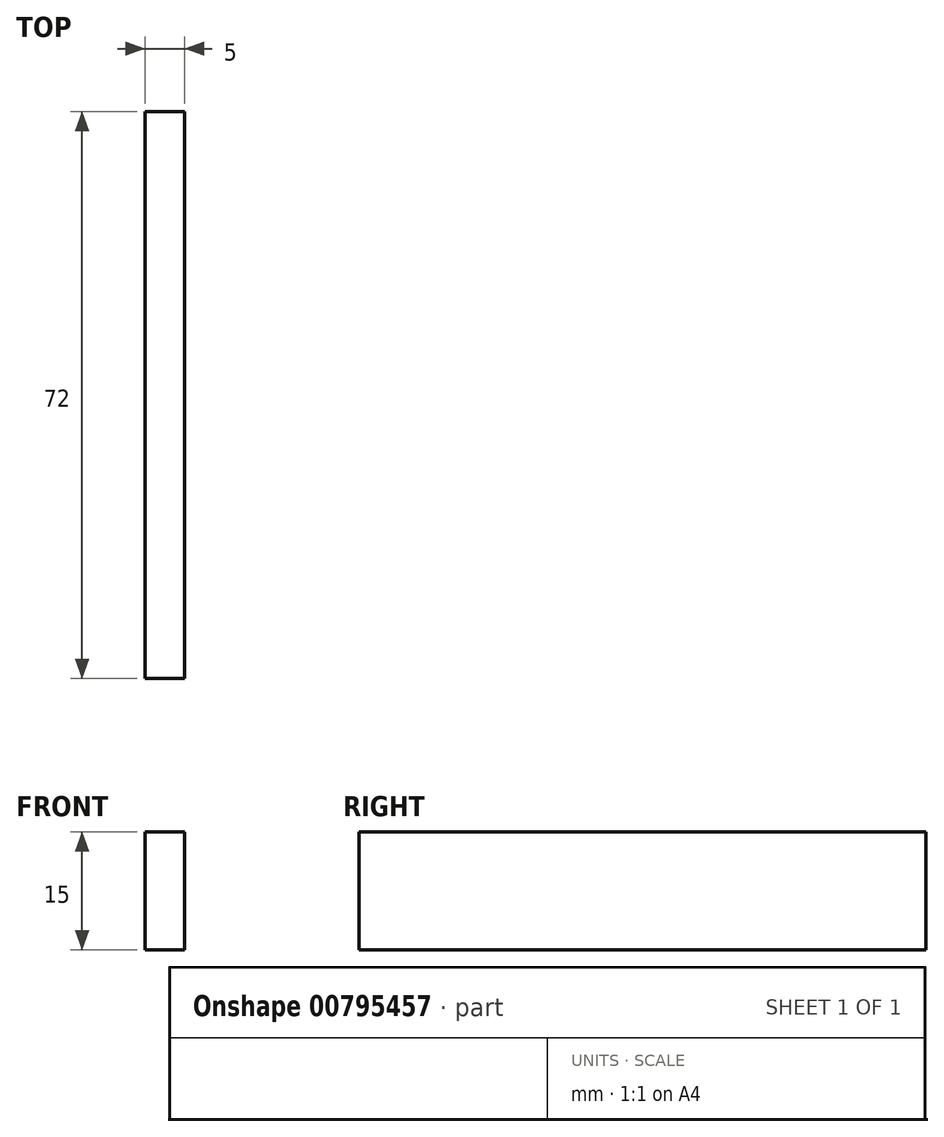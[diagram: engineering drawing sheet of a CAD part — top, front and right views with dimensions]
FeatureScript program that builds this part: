
annotation { "Feature Type Name" : "Feature", "Feature Type Description" : "" }
export const myFeature = defineFeature(function(context is Context, id is Id, definition is map)
    precondition{}
    {
        {
            var Q0;
            Q0=qCreatedBy(makeId("Front.planeOp"),FACE);
            var sketch = newSketch(context, id + "F0", { "sketchPlane" : qUnion([Q0])});
            skLineSegment(sketch, "E0.bottom", {"start": v(2.5, 7.5) * mm, "end": v(-2.5, 7.5) * mm});
            skLineSegment(sketch, "E0.top", {"start": v(2.5, -7.5) * mm, "end": v(-2.5, -7.5) * mm});
            skLineSegment(sketch, "E0.left", {"start": v(2.5, 7.5) * mm, "end": v(2.5, -7.5) * mm});
            skLineSegment(sketch, "E0.right", {"start": v(-2.5, 7.5) * mm, "end": v(-2.5, -7.5) * mm});
            skPoint(sketch, "E0.middle", {"position": v(0, 0) * mm});
            skSolve(sketch);
        }
        {
            var Q0;
            Q0=makeQuery(id+"F0.imprint","IMPRINT",FACE,{"disambiguationData":[TD([[makeQuery(id+"F0.imprint","IMPRINT",EDGE,{"derivedFrom":sQuery(id+"F0.wireOp",EDGE,"E0.bottom")}),1.0]])]});
            extrude(context, id + "F1", {"entities" : qUnion([Q0]), "depth" : 72 * mm, "offsetDistance" : 25 * mm});
        }
        {
            var Q0;
            Q0=makeQuery(id+"F0.imprint","IMPRINT",FACE,{"disambiguationData":[TD([[makeQuery(id+"F0.imprint","IMPRINT",EDGE,{"derivedFrom":sQuery(id+"F0.wireOp",EDGE,"E0.bottom")}),1.0]])]});
            extrude(context, id + "F2", {"entities" : qUnion([Q0]), "operationType" : NewBodyOperationType.ADD, "depth" : 72 * mm, "offsetDistance" : 25 * mm});
        }
        {
            var Q0;
            Q0=qSketchRegion(id+"F0",true);
            extrude(context, id + "F3", {"entities" : qUnion([Q0]), "operationType" : NewBodyOperationType.ADD, "depth" : 72 * mm, "offsetDistance" : 25 * mm});
        }
    });
